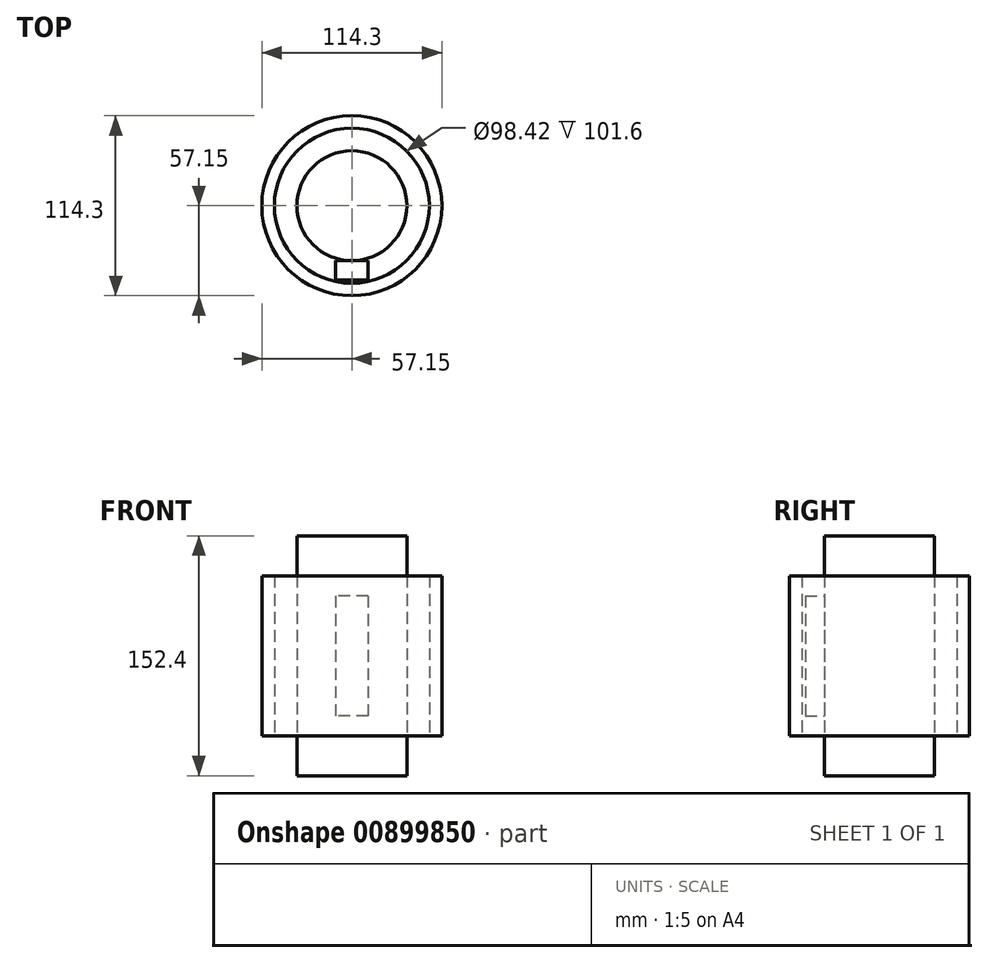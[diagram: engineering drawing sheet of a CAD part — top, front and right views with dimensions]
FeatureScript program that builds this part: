
annotation { "Feature Type Name" : "Feature", "Feature Type Description" : "" }
export const myFeature = defineFeature(function(context is Context, id is Id, definition is map)
    precondition{}
    {
        {
            var Q0;
            Q0=qCreatedBy(makeId("Top.planeOp"),FACE);
            var sketch = newSketch(context, id + "F0", { "sketchPlane" : qUnion([Q0])});
            skCircle(sketch, "E0", {"center": v(0, 0) * mm, "radius": 34.93 * mm});
            skSolve(sketch);
        }
        {
            var Q0;
            Q0=makeQuery(id+"F0.imprint","IMPRINT",FACE,{"disambiguationData":[TD([[makeQuery(id+"F0.imprint","IMPRINT",EDGE,{"derivedFrom":sQuery(id+"F0.wireOp",EDGE,"E0")}),1.0]])]});
            extrude(context, id + "F1", {"entities" : qUnion([Q0]), "endBound" : BoundingType.SYMMETRIC, "depth" : 152.4 * mm, "offsetDistance" : 25.4 * mm});
        }
        {
            var Q0;
            Q0=qCreatedBy(makeId("Top.planeOp"),FACE);
            var sketch = newSketch(context, id + "F2", { "sketchPlane" : qUnion([Q0])});
            skCircle(sketch, "E1", {"center": v(0, 0) * mm, "radius": 49.21 * mm});
            skCircle(sketch, "E2", {"center": v(0, 0) * mm, "radius": 57.15 * mm});
            skSolve(sketch);
        }
        {
            var Q0;
            Q0 = qSketchRegion(id + "F2", true);
            extrude(context, id + "F3", {"entities" : qUnion([Q0]), "endBound" : BoundingType.SYMMETRIC, "depth" : 101.6 * mm, "offsetDistance" : 25.4 * mm});
        }
        {
            var Q0;
            Q0=qCreatedBy(makeId("Front.planeOp"),FACE);
            cPlane(context, id + "F4", {"entities" : qUnion([Q0]), "cplaneType" : CPlaneType.OFFSET, "offset" : 34.92 * mm, "width" : 152.4 * mm, "height" : 152.4 * mm});
        }
        {
            var Q0;
            Q0=qCreatedBy(id+"F4.planeOp",FACE);
            var sketch = newSketch(context, id + "F5", { "sketchPlane" : qUnion([Q0])});
            skLineSegment(sketch, "E3.bottom", {"start": v(10.41, 38.1) * mm, "end": v(-10.41, 38.1) * mm});
            skLineSegment(sketch, "E3.top", {"start": v(10.41, -38.1) * mm, "end": v(-10.41, -38.1) * mm});
            skLineSegment(sketch, "E3.left", {"start": v(10.41, 38.1) * mm, "end": v(10.41, -38.1) * mm});
            skLineSegment(sketch, "E3.right", {"start": v(-10.41, 38.1) * mm, "end": v(-10.41, -38.1) * mm});
            skPoint(sketch, "E3.middle", {"position": v(0, 0) * mm});
            skSolve(sketch);
        }
        {
            var Q0;
            Q0 = qSketchRegion(id + "F5", true);
            extrude(context, id + "F6", {"entities" : qUnion([Q0]), "depth" : 12.24 * mm, "offsetDistance" : 25.4 * mm});
        }
    });
